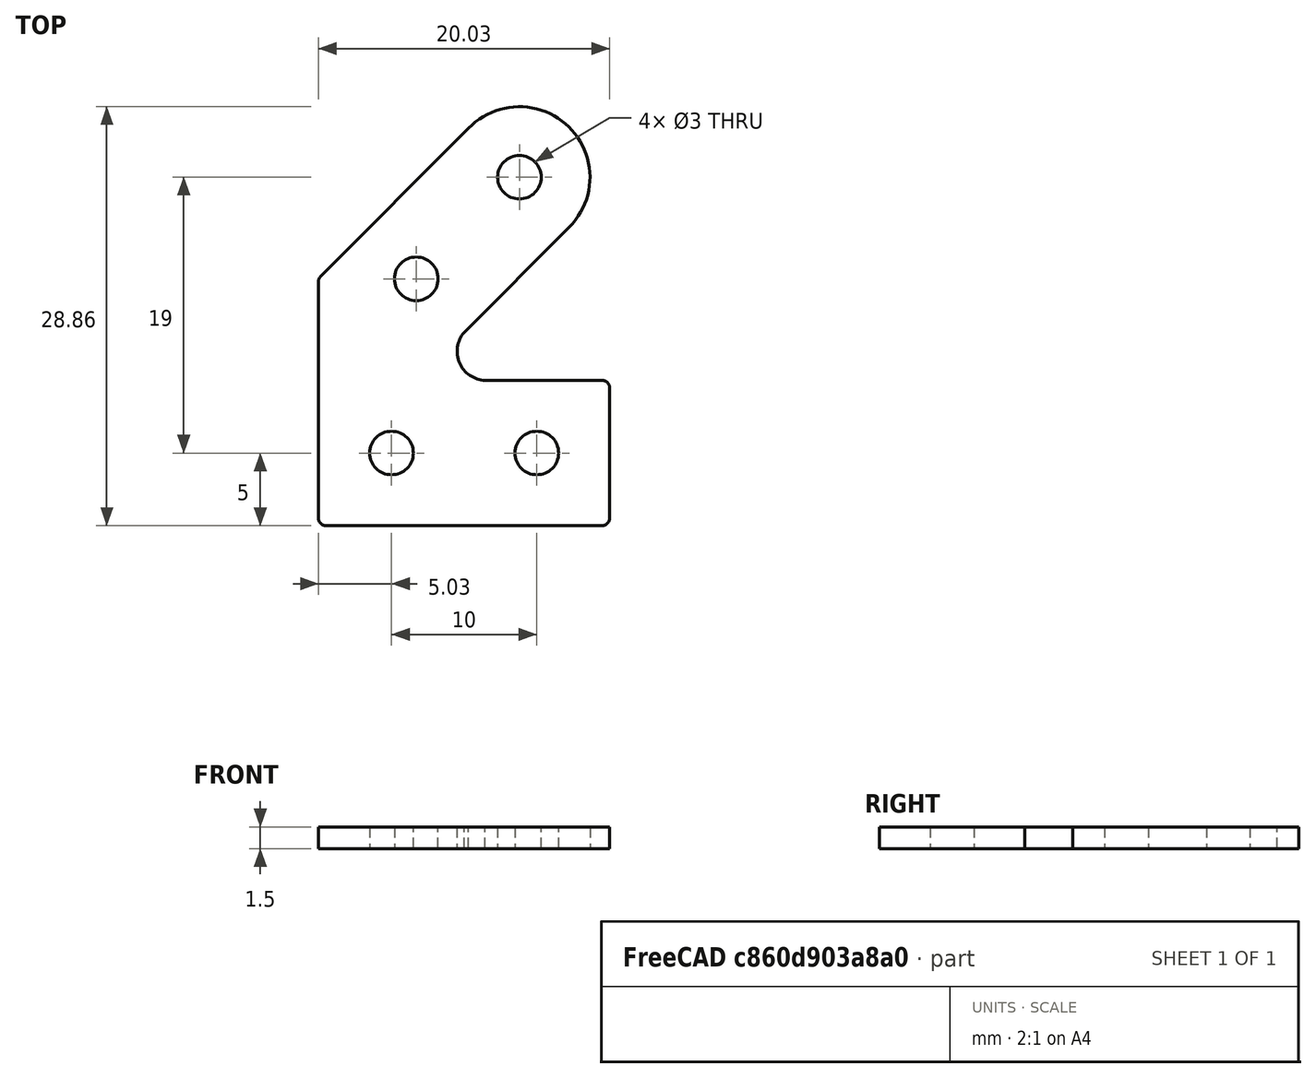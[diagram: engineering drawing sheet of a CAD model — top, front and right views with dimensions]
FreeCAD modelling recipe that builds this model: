
FCSTD DOCUMENT  (FreeCAD 0.18R16146 (Git))
Label: makerbeam_bracket_45degree
License: All rights reserved
LicenseURL: http://en.wikipedia.org/wiki/All_rights_reserved
objects: Sketcher::SketchObject×1, PartDesign::Pad×1, PartDesign::Fillet×1, PartDesign::Body×1
note: 5 computed .brp shape members not serialized (recipe doc carries the construction recipe); baked Part::Feature solids carry a one-line shape summary decoded from their .brp

FEATURE [Sketcher::SketchObject] Sketch
  MapMode = 5
  Support = -> [XY_Plane]
  sketch-geometry (12):
    g0: Circle CenterX=-5 CenterY=5 CenterZ=0 NormalX=0 NormalY=0 NormalZ=1 AngleXU=0 Radius=1.5
    g1: Circle CenterX=-15 CenterY=5 CenterZ=0 NormalX=0 NormalY=0 NormalZ=1 AngleXU=0 Radius=1.5
    g2: Circle CenterX=-13.3 CenterY=17 CenterZ=0 NormalX=0 NormalY=0 NormalZ=1 AngleXU=0 Radius=1.5
    g3: Circle CenterX=-6.2 CenterY=24 CenterZ=0 NormalX=0 NormalY=0 NormalZ=1 AngleXU=0 Radius=1.5
    g4: LineSegment StartX=0 StartY=0 StartZ=0 EndX=-20.0251 EndY=0 EndZ=0
    g5: LineSegment StartX=-20.0251 StartY=0 StartZ=0 EndX=-20.0251 EndY=17.0251 EndZ=0
    g6: LineSegment StartX=-20.0251 StartY=17.0251 StartZ=0 EndX=-9.70195 EndY=27.3642 EndZ=0
    g7: LineSegment StartX=0 StartY=0 StartZ=0 EndX=0 EndY=10.0042 EndZ=0
    g8: LineSegment StartX=0 StartY=10.0042 StartZ=0 EndX=-8.56249 EndY=10.0042 EndZ=0
    g9: LineSegment StartX=-10 StartY=13.3067 StartZ=0 EndX=-2.76056 EndY=20.5719 EndZ=0
    g10: ArcOfCircle CenterX=-6.2 CenterY=24 CenterZ=0 NormalX=0 NormalY=0 NormalZ=1 AngleXU=0 Radius=4.85609 StartAngle=5.49944 EndAngle=8.65944
    g11: ArcOfCircle CenterX=-8.49403 CenterY=11.9981 CenterZ=0 NormalX=0 NormalY=0 NormalZ=1 AngleXU=0 Radius=1.9951 StartAngle=2.42619 EndAngle=4.67807
  constraints (21):
    c: DistanceX(g0,g-1) = 5
    c: DistanceY(g-1,g0) = 5
    c: DistanceX(g1,g-1) = 15
    c: DistanceX(g2,g-1) = 13.3
    c: DistanceY(g-1,g2) = 17
    c: DistanceX(g3,g-1) = 6.2
    c: DistanceY(g-1,g3) = 24
    c: Coincident(g-1,g4)
    c: PointOnObject(g4,g-1)
    c: Coincident(g4,g5)
    c: Vertical(g5)
    c: Coincident(g5,g6)
    c: Coincident(g4,g7)
    c: PointOnObject(g7,g-2)
    c: Coincident(g7,g8)
    c: Horizontal(g8)
    c: Coincident(g10,g3)
    c: Coincident(g6,g10)
    c: Coincident(g9,g10)
    c: Coincident(g8,g11)
    c: Coincident(g11,g9)
FEATURE [PartDesign::Pad] Pad
  Length = 1.5
  Length2 = 100
  Profile = -> Sketch
  Type = 0
FEATURE [PartDesign::Fillet] Fillet
  Base = -> Pad [Edge5,Edge8,Edge11,Edge14]
  BaseFeature = -> Pad
  Radius = 0.5
FEATURE [PartDesign::Body] Body  label="makerbeam_bracket_45degree"
  Group = -> [Sketch,Pad,Fillet]
  Origin = -> Origin
  Tip = -> Fillet
